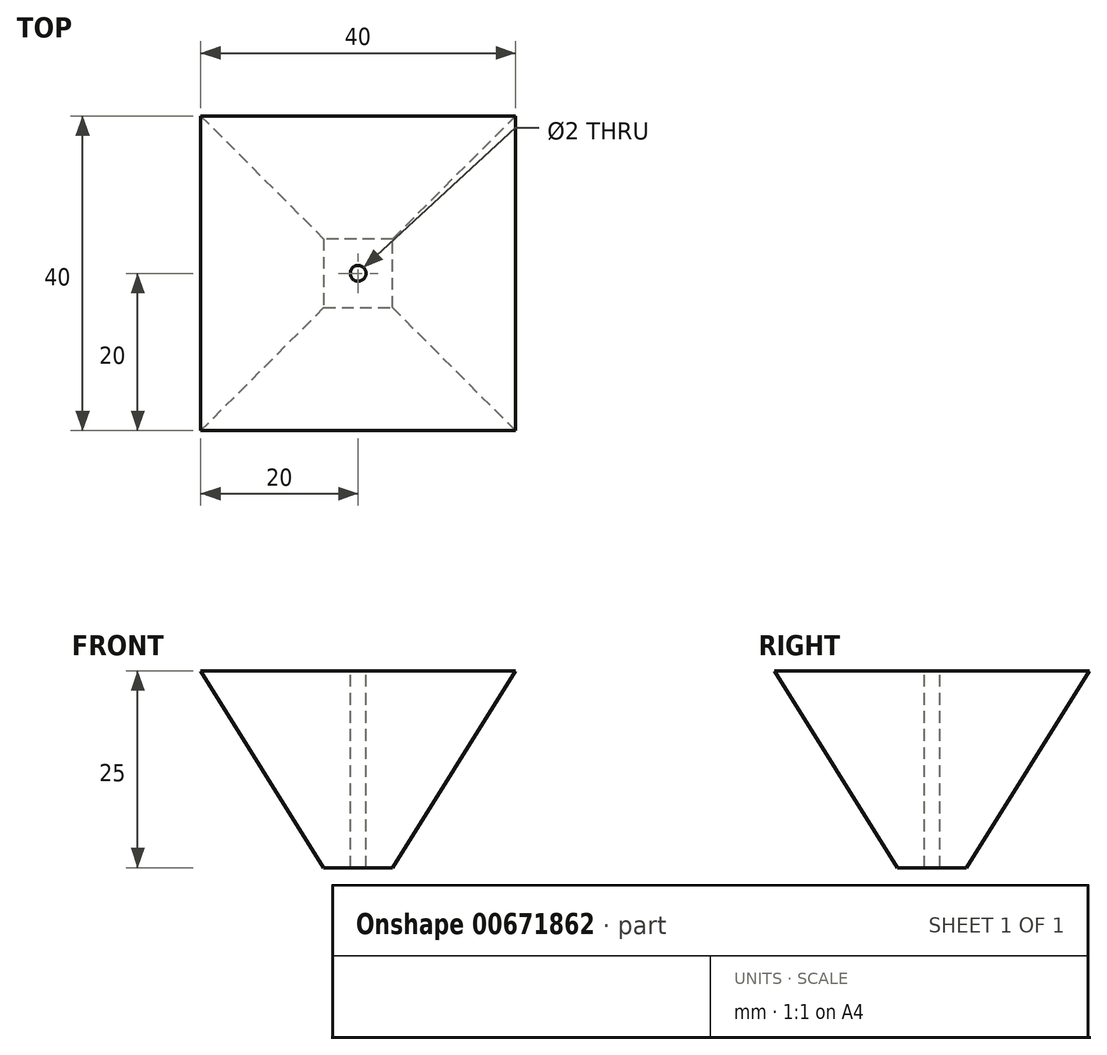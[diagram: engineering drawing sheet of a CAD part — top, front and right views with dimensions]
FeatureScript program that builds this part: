
annotation { "Feature Type Name" : "Feature", "Feature Type Description" : "" }
export const myFeature = defineFeature(function(context is Context, id is Id, definition is map)
    precondition{}
    {
        {
            var Q0;
            Q0=qCreatedBy(makeId("Top.planeOp"),FACE);
            var sketch = newSketch(context, id + "F0", { "sketchPlane" : qUnion([Q0])});
            skLineSegment(sketch, "E0.bottom", {"start": v(20, -20) * mm, "end": v(-20, -20) * mm});
            skLineSegment(sketch, "E0.top", {"start": v(20, 20) * mm, "end": v(-20, 20) * mm});
            skLineSegment(sketch, "E0.left", {"start": v(20, -20) * mm, "end": v(20, 20) * mm});
            skLineSegment(sketch, "E0.right", {"start": v(-20, -20) * mm, "end": v(-20, 20) * mm});
            skPoint(sketch, "E0.middle", {"position": v(0, 0) * mm});
            skSolve(sketch);
        }
        {
            var Q0;
            Q0=makeQuery(id+"F0.imprint","IMPRINT",FACE,{"disambiguationData":[TD([[makeQuery(id+"F0.imprint","IMPRINT",EDGE,{"derivedFrom":sQuery(id+"F0.wireOp",EDGE,"E0.bottom")}),-1.0]])]});
            extrude(context, id + "F1", {"entities" : qUnion([Q0]), "oppositeDirection" : true, "depth" : 25 * mm, "offsetDistance" : 25 * mm, "hasDraft" : true, "draftAngle" : 32 * degree, "draftPullDirection" : true});
        }
        {
            var Q0;
            Q0=sQuery(id+"F0.wireOp",VERTEX,"E0.middle");
            var Q1;
            Q1=makeQuery(id+"F1.opExtrude","SWEPT_BODY",BODY,{"disambiguationData":[OSD([sQuery(id+"F0.wireOp",EDGE,"E0.bottom"),sQuery(id+"F0.wireOp",EDGE,"E0.top"),sQuery(id+"F0.wireOp",EDGE,"E0.left"),sQuery(id+"F0.wireOp",EDGE,"E0.right")])]});
            hole(context, id + "F2", {"style" : HoleStyle.SIMPLE, "endStyle" : HoleEndStyle.THROUGH, "holeDiameter" : 2 * mm, "majorDiameter" : 5 * mm, "isTappedThrough" : true, "tappedDepth" : 12 * mm, "tapClearance" : 3, "locations" : qUnion([Q0]), "scope" : qUnion([Q1])});
        }
    });
